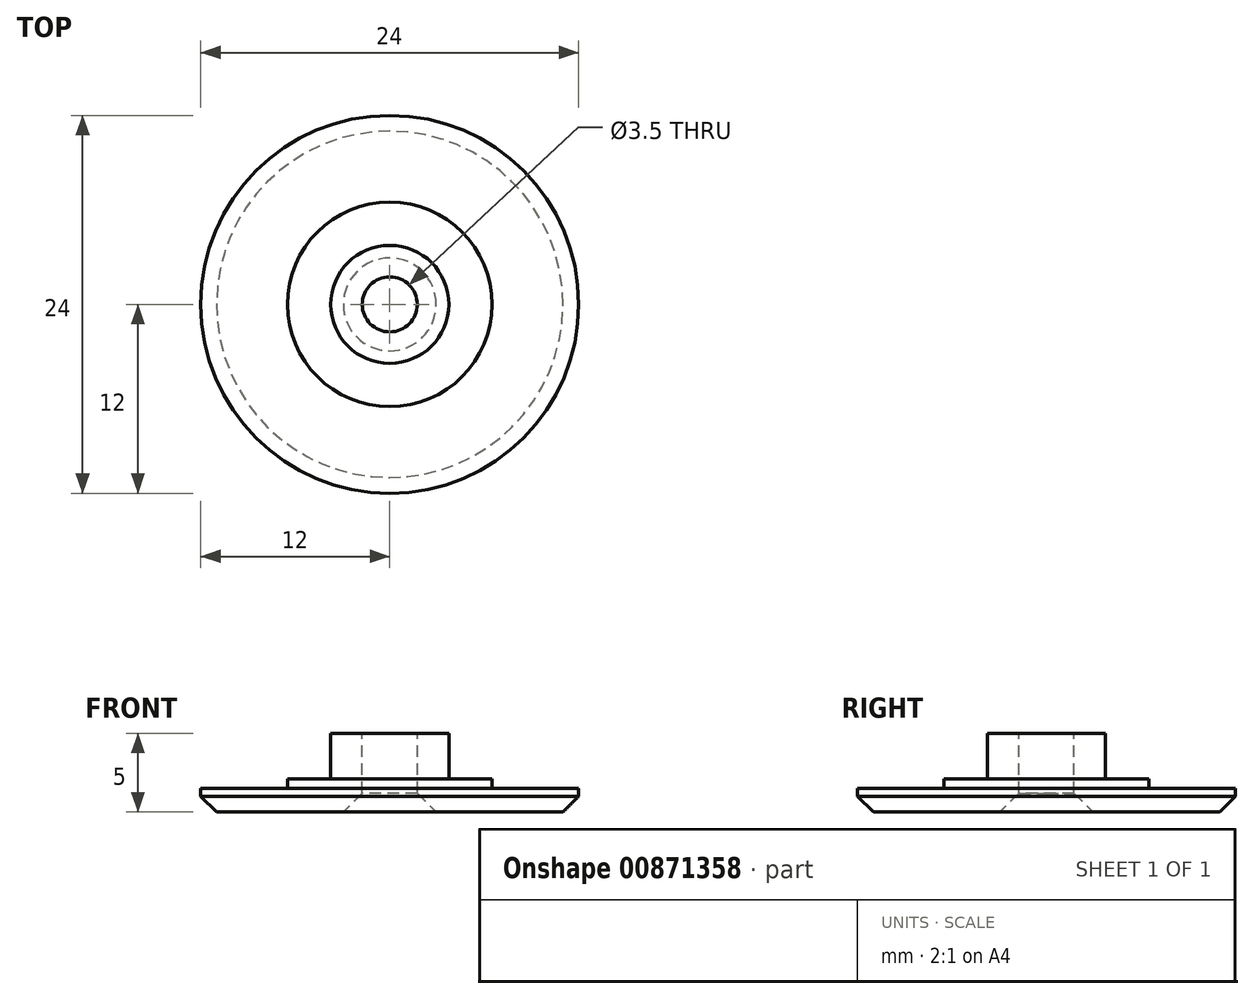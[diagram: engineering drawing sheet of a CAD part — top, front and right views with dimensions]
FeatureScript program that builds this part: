
annotation { "Feature Type Name" : "Feature", "Feature Type Description" : "" }
export const myFeature = defineFeature(function(context is Context, id is Id, definition is map)
    precondition{}
    {
        {
            var Q0;
            Q0=qCreatedBy(makeId("Top.planeOp"),FACE);
            var sketch = newSketch(context, id + "F0", { "sketchPlane" : qUnion([Q0])});
            skCircle(sketch, "E0", {"center": v(0, 0) * mm, "radius": 12 * mm});
            skCircle(sketch, "E1", {"center": v(0, 0) * mm, "radius": 3.75 * mm});
            skCircle(sketch, "E2", {"center": v(0, 0) * mm, "radius": 1.75 * mm});
            skCircle(sketch, "E3", {"center": v(0, 0) * mm, "radius": 6.5 * mm});
            skSolve(sketch);
        }
        {
            var Q0;
            Q0=makeQuery(id+"F0.imprint","IMPRINT",FACE,{"disambiguationData":[TD([[makeQuery(id+"F0.imprint","IMPRINT",EDGE,{"derivedFrom":sQuery(id+"F0.wireOp",EDGE,"E0")}),1.0]])]});
            var Q1;
            Q1=makeQuery(id+"F0.imprint","IMPRINT",FACE,{"disambiguationData":[TD([[makeQuery(id+"F0.imprint","IMPRINT",EDGE,{"derivedFrom":sQuery(id+"F0.wireOp",EDGE,"E1")}),1.0]])]});
            var Q2;
            Q2=makeQuery(id+"F0.imprint","IMPRINT",FACE,{"disambiguationData":[TD([[makeQuery(id+"F0.imprint","IMPRINT",EDGE,{"derivedFrom":sQuery(id+"F0.wireOp",EDGE,"E1")}),-1.0]])]});
            extrude(context, id + "F1", {"entities" : qUnion([Q0, Q1, Q2]), "oppositeDirection" : true, "depth" : 1.5 * mm, "offsetDistance" : 25 * mm});
        }
        {
            var Q0;
            Q0=makeQuery(id+"F0.imprint","IMPRINT",FACE,{"disambiguationData":[TD([[makeQuery(id+"F0.imprint","IMPRINT",EDGE,{"derivedFrom":sQuery(id+"F0.wireOp",EDGE,"E1")}),1.0]])]});
            extrude(context, id + "F2", {"entities" : qUnion([Q0]), "operationType" : NewBodyOperationType.ADD, "depth" : 3.5 * mm, "offsetDistance" : 25 * mm});
        }
        {
            var Q0;
            Q0=makeQuery(id+"F0.imprint","IMPRINT",FACE,{"disambiguationData":[TD([[makeQuery(id+"F0.imprint","IMPRINT",EDGE,{"derivedFrom":sQuery(id+"F0.wireOp",EDGE,"E1")}),-1.0]])]});
            extrude(context, id + "F3", {"entities" : qUnion([Q0]), "operationType" : NewBodyOperationType.ADD, "depth" : 0.6 * mm, "offsetDistance" : 25 * mm});
        }
        {
            var Q0;
            Q0=makeQuery(id+"F1.opExtrude","CAP_EDGE",EDGE,{"disambiguationData":[OSD([sQuery(id+"F0.wireOp",EDGE,"E0")])],"isStart":false});
            chamfer(context, id + "F4", {"entities" : qUnion([Q0]), "width" : 1 * mm, "tangentPropagation" : true});
        }
        {
            var Q0;
            Q0=makeQuery(id+"F1.opExtrude","CAP_EDGE",EDGE,{"disambiguationData":[OSD([sQuery(id+"F0.wireOp",EDGE,"E2")])],"isStart":false});
            chamfer(context, id + "F5", {"entities" : qUnion([Q0]), "width" : 1.2 * mm, "tangentPropagation" : true});
        }
    });
